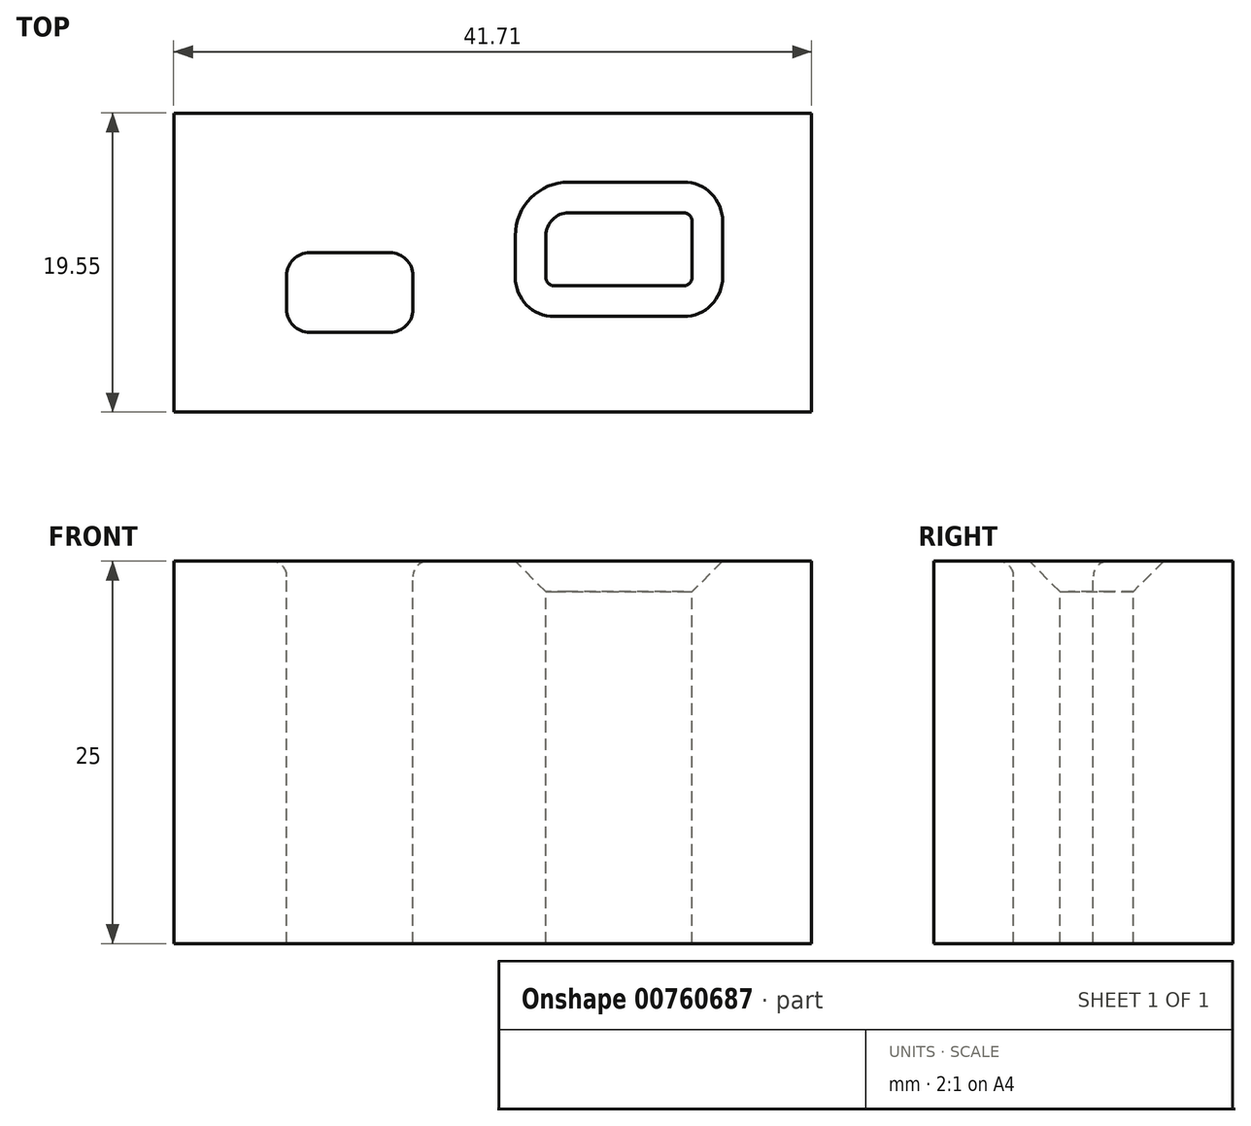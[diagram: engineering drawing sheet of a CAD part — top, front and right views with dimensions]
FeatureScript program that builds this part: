
annotation { "Feature Type Name" : "Feature", "Feature Type Description" : "" }
export const myFeature = defineFeature(function(context is Context, id is Id, definition is map)
    precondition{}
    {
        {
            var Q0;
            Q0=qCreatedBy(makeId("Top.planeOp"),FACE);
            var sketch = newSketch(context, id + "F0", { "sketchPlane" : qUnion([Q0])});
            skLineSegment(sketch, "E0.bottom", {"start": v(-49.86, 46.7) * mm, "end": v(-8.15, 46.7) * mm});
            skLineSegment(sketch, "E0.top", {"start": v(-49.86, 27.16) * mm, "end": v(-8.15, 27.16) * mm});
            skLineSegment(sketch, "E0.left", {"start": v(-49.86, 46.7) * mm, "end": v(-49.86, 27.16) * mm});
            skLineSegment(sketch, "E0.right", {"start": v(-8.15, 46.7) * mm, "end": v(-8.15, 27.16) * mm});
            skLineSegment(sketch, "E1.bottom", {"start": v(-42.47, 37.58) * mm, "end": v(-34.22, 37.58) * mm});
            skLineSegment(sketch, "E1.top", {"start": v(-42.47, 32.37) * mm, "end": v(-34.22, 32.37) * mm});
            skLineSegment(sketch, "E1.left", {"start": v(-42.47, 37.58) * mm, "end": v(-42.47, 32.37) * mm});
            skLineSegment(sketch, "E1.right", {"start": v(-34.22, 37.58) * mm, "end": v(-34.22, 32.37) * mm});
            skLineSegment(sketch, "E2.bottom", {"start": v(-25.53, 40.19) * mm, "end": v(-15.97, 40.19) * mm});
            skLineSegment(sketch, "E2.top", {"start": v(-25.53, 35.41) * mm, "end": v(-15.97, 35.41) * mm});
            skLineSegment(sketch, "E2.left", {"start": v(-25.53, 40.19) * mm, "end": v(-25.53, 35.41) * mm});
            skLineSegment(sketch, "E2.right", {"start": v(-15.97, 40.19) * mm, "end": v(-15.97, 35.41) * mm});
            skSolve(sketch);
        }
        {
            var Q0;
            Q0 = qSketchRegion(id + "F0", true);
            extrude(context, id + "F1", {"entities" : qUnion([Q0]), "depth" : -25 * mm, "offsetDistance" : 25 * mm});
        }
        {
            var Q0;
            Q0=makeQuery(id+"F1.opExtrude","SWEPT_EDGE",EDGE,{"disambiguationData":[OSD([sQuery(id+"F0.wireOp",EDGE,"E1.bottom"),sQuery(id+"F0.wireOp",EDGE,"E1.left")])]});
            var Q1;
            Q1=makeQuery(id+"F1.opExtrude","SWEPT_EDGE",EDGE,{"disambiguationData":[OSD([sQuery(id+"F0.wireOp",EDGE,"E1.bottom"),sQuery(id+"F0.wireOp",EDGE,"E1.right")])]});
            var Q2;
            Q2=makeQuery(id+"F1.opExtrude","SWEPT_EDGE",EDGE,{"disambiguationData":[OSD([sQuery(id+"F0.wireOp",EDGE,"E1.top"),sQuery(id+"F0.wireOp",EDGE,"E1.left")])]});
            var Q3;
            Q3=makeQuery(id+"F1.opExtrude","SWEPT_EDGE",EDGE,{"disambiguationData":[OSD([sQuery(id+"F0.wireOp",EDGE,"E1.top"),sQuery(id+"F0.wireOp",EDGE,"E1.right")])]});
            var Q4;
            Q4=makeQuery(id+"F1.opExtrude","SWEPT_EDGE",EDGE,{"disambiguationData":[OSD([sQuery(id+"F0.wireOp",EDGE,"E2.bottom"),sQuery(id+"F0.wireOp",EDGE,"E2.left")])]});
            fillet(context, id + "F2", {"entities" : qUnion([Q0, Q1, Q2, Q3, Q4]), "radius" : 1.5 * mm, "tangentPropagation" : true, "allowEdgeOverflow" : false});
        }
        {
            var Q0;
            Q0=makeQuery(id+"F1.opExtrude","SWEPT_EDGE",EDGE,{"disambiguationData":[OSD([sQuery(id+"F0.wireOp",EDGE,"E2.bottom"),sQuery(id+"F0.wireOp",EDGE,"E2.right")])]});
            var Q1;
            Q1=makeQuery(id+"F1.opExtrude","SWEPT_EDGE",EDGE,{"disambiguationData":[OSD([sQuery(id+"F0.wireOp",EDGE,"E2.top"),sQuery(id+"F0.wireOp",EDGE,"E2.left")])]});
            var Q2;
            Q2=makeQuery(id+"F1.opExtrude","SWEPT_EDGE",EDGE,{"disambiguationData":[OSD([sQuery(id+"F0.wireOp",EDGE,"E2.top"),sQuery(id+"F0.wireOp",EDGE,"E2.right")])]});
            fillet(context, id + "F3", {"entities" : qUnion([Q0, Q1, Q2]), "radius" : 0.55 * mm, "tangentPropagation" : true, "allowEdgeOverflow" : false});
        }
        {
            var Q0;
            Q0=makeQuery(id+"F1.opExtrude","CAP_EDGE",EDGE,{"disambiguationData":[OSD([sQuery(id+"F0.wireOp",EDGE,"E1.bottom")])],"isStart":true});
            fillet(context, id + "F4", {"entities" : qUnion([Q0]), "radius" : 1 * mm, "tangentPropagation" : true, "allowEdgeOverflow" : false});
        }
        {
            var Q0;
            Q0=makeQuery(id+"F1.opExtrude","CAP_EDGE",EDGE,{"disambiguationData":[OSD([sQuery(id+"F0.wireOp",EDGE,"E2.bottom")])],"isStart":true});
            chamfer(context, id + "F5", {"entities" : qUnion([Q0]), "width" : 2 * mm, "tangentPropagation" : true});
        }
    });
